FCSTD DOCUMENT  (FreeCAD 0.18.4R)
Label: E3D-V6-Titan-Radial-Fan-Heatbreak-Cooler
License: All rights reserved
LicenseURL: http://en.wikipedia.org/wiki/All_rights_reserved
objects: Sketcher::SketchObject×27, Part::Feature×23, Part::Mirroring×20, PartDesign::Pad×16, PartDesign::Plane×13, PartDesign::Pocket×8, PartDesign::ShapeBinder×8, PartDesign::Body×7, App::Part×5, App::DocumentObjectGroup×3, PartDesign::FeatureBase×3, PartDesign::Fillet×2, Part::Loft×1, PartDesign::AdditiveLoft×1, Mesh::Feature×1, Part::FeaturePython×1
note: 155 computed .brp shape members not serialized (recipe doc carries the construction recipe); baked Part::Feature solids carry a one-line shape summary decoded from their .brp

FEATURE [Sketcher::SketchObject] Sketch
  MapMode = 5
  Support = -> [XY_Plane]
  sketch-geometry (10):
    g0: LineSegment StartX=-15 StartY=15 StartZ=0 EndX=15 EndY=15 EndZ=0
    g1: LineSegment StartX=15 StartY=15 StartZ=0 EndX=15 EndY=-15 EndZ=0
    g2: LineSegment StartX=15 StartY=-15 StartZ=0 EndX=-15 EndY=-15 EndZ=0
    g3: LineSegment StartX=-15 StartY=-15 StartZ=0 EndX=-15 EndY=15 EndZ=0
    g4: LineSegment [constr] StartX=-15 StartY=15 StartZ=0 EndX=15 EndY=-15 EndZ=0
    g5: LineSegment [constr] StartX=15 StartY=15 StartZ=0 EndX=-15 EndY=-15 EndZ=0
    g6: Circle CenterX=-12.125 CenterY=12.125 CenterZ=0 NormalX=0 NormalY=0 NormalZ=1 AngleXU=0 Radius=1.5
    g7: Circle CenterX=12.125 CenterY=12.125 CenterZ=0 NormalX=0 NormalY=0 NormalZ=1 AngleXU=0 Radius=1.5
    g8: Circle CenterX=12.125 CenterY=-12.125 CenterZ=0 NormalX=0 NormalY=0 NormalZ=1 AngleXU=0 Radius=1.5
    g9: Circle CenterX=-12.125 CenterY=-12.125 CenterZ=0 NormalX=0 NormalY=0 NormalZ=1 AngleXU=0 Radius=1.5
  constraints (25):
    c: Coincident(g0,g1)
    c: Coincident(g1,g2)
    c: Coincident(g2,g3)
    c: Coincident(g3,g0)
    c: Horizontal(g2)
    c: Vertical(g1)
    c: Symmetric(g0,g0,g-2)
    c: Symmetric(g2,g0,g-1)
    c: DistanceX(g0,g0) = 30  'Lüfterlänge'
    c: Equal(g3,g0)
    c: Coincident(g4,g0)
    c: Coincident(g4,g1)
    c: Coincident(g5,g0)
    c: Coincident(g5,g2)
    c: PointOnObject(g6,g4)
    c: PointOnObject(g8,g4)
    c: PointOnObject(g9,g5)
    c: Distance(g7,g6) = 24.25
    c: Diameter(g6) = 3
    c: Equal(g6,g7)
    c: Equal(g6,g8)
    c: Equal(g6,g9)
    c: Symmetric(g7,g6,g-2)
    c: Distance(g9,g6) = 24.25
    c: Distance(g8,g9) = 24.25
FEATURE [PartDesign::Pad] Pad
  Length = 12
  Length2 = 100
  Profile = -> Sketch
  Type = 0
FEATURE [Sketcher::SketchObject] Sketch001
  MapMode = 5
  Support = -> [XY_Plane]
  sketch-geometry (1):
    g0: Circle CenterX=0 CenterY=0 CenterZ=0 NormalX=0 NormalY=0 NormalZ=1 AngleXU=0 Radius=13.25
  constraints (2):
    c: Coincident(g0,g-1)
    c: Diameter(g0) = 26.5
FEATURE [PartDesign::Pocket] Pocket
  BaseFeature = -> Pad
  Length = 10
  Length2 = 100
  Profile = -> Sketch001
  Reversed = true
  Type = 0
  expr: Length = Pad.Length - 2mm
FEATURE [PartDesign::Plane] DatumPlane
  AttachmentOffset = pos=(0,0,15) rot=(0,0,1;0rad)
  Length = 35.1381
  MapMode = 5
  Placement = pos=(15,-3.3e-15,3.3e-15) rot=(0.57735,0.57735,0.57735;2.0944rad)
  ResizeMode = 0
  Support = -> [YZ_Plane]
  Width = 27.1381
  expr: AttachmentOffset.Base.z = Sketch.Constraints.Lüfterlänge / 2
FEATURE [Sketcher::SketchObject] Sketch002
  ExternalGeometry = -> [Sketch]
  MapMode = 5
  Placement = pos=(15,-3.3e-15,3.3e-15) rot=(0.57735,0.57735,0.57735;2.0944rad)
  Support = -> [DatumPlane]
  expr: Constraints[9] = Pad.Length - 2 * Constraints.Wandstärke
  sketch-geometry (4):
    g0: LineSegment StartX=-10 StartY=10 StartZ=0 EndX=10 EndY=10 EndZ=0
    g1: LineSegment StartX=10 StartY=10 StartZ=0 EndX=10 EndY=1 EndZ=0
    g2: LineSegment StartX=10 StartY=1 StartZ=0 EndX=-10 EndY=1 EndZ=0
    g3: LineSegment StartX=-10 StartY=1 StartZ=0 EndX=-10 EndY=10 EndZ=0
  constraints (11):
    c: Coincident(g0,g1)
    c: Coincident(g2,g3)
    c: Coincident(g3,g0)
    c: Horizontal(g0)
    c: Vertical(g1)
    c: Vertical(g3)
    c: DistanceX(g2,g2) = 20
    c: Symmetric(g2,g1,g-2)
    c: Coincident(g2,g1)
    c: DistanceY(g-4,g0) = 10
    c: DistanceY(g-3,g1) = 1  'Wandstärke'
FEATURE [PartDesign::Pocket] Pocket001
  BaseFeature = -> Pocket
  Length = 6.5
  Length2 = 100
  Profile = -> Sketch002
  Type = 0
FEATURE [PartDesign::Body] Body  label="30mm-Fan-Adapter"
  Group = -> [Sketch,Pad,Sketch001,Pocket,DatumPlane,Sketch002,Pocket001]
  Origin = -> Origin
  Tip = -> Pocket001
FEATURE [PartDesign::ShapeBinder] ShapeBinder  label="ShapeBinder_30mm_Fan_Adapter"
  Support = -> [Pocket001]
  TraceSupport = false
FEATURE [PartDesign::ShapeBinder] ShapeBinder002
  Placement = pos=(-68,-32,-2e-15) rot=(1,0,0;1.5708rad)
  TraceSupport = false
FEATURE [App::DocumentObjectGroup] Group  label="3rd-party"
FEATURE [Part::Feature] Part__Feature008  label="M_BEARING_MR95ZZ"
  Placement = pos=(22.2171,-38.5563,-4) rot=(0.707107,0.000752,0.707107;3.1431rad)
  shape: bbox 9.742 x 9.742 x 3 mm, 55 faces, 13 solids (baked)
FEATURE [Part::Feature] Part__Feature020  label="ISO 4762 - M3 x 25ISO"
  Placement = pos=(28.5171,-8.05,-25) rot=(0,-1,0;1.5708rad)
  shape: bbox 5.953 x 5.953 x 28 mm, 15 faces (baked)
FEATURE [Part::Mirroring] Part__Mirroring013  label="ISO 4762 - M3 x 25ISO (Mirror #14)"
  Base = (0,0,0)
  Normal = (1,0,0)
  Source = -> Part__Feature020
FEATURE [Part::Feature] Part__Feature009  label="M_BEARING_SMR74ZZ"
  Placement = pos=(22.2171,-38.5563,-20.75) rot=(0,1,0;1.5708rad)
  shape: bbox 9.742 x 9.742 x 3 mm, 55 faces, 13 solids (baked)
FEATURE [Part::Feature] Part__Feature014  label="EX_PIGNION"
  Placement = pos=(6.66075,-23,-0.4) rot=(-0.998967,-0.032133,0.032133;1.57183rad)
  shape: bbox 12.06 x 11.99 x 9 mm, 97 faces (baked)
FEATURE [Part::Feature] Part__Feature003  label="EX_EXTRUDER_LID (Edition 4)_Public"
  Placement = pos=(0.461723,-9.23586,-22) rot=(1,0,0;3.14159rad)
  shape: bbox 46.39 x 49.51 x 137 mm, 484 faces (baked)
FEATURE [Part::Feature] Part__Feature001  label="Spur Gear21"
  Placement = pos=(0,22,0) rot=(0,0,1;3.09399rad)
  shape: bbox 34 x 33.98 x 4 mm, 267 faces (baked)
FEATURE [Part::Mirroring] Part__Mirroring016  label="Spur Gear21 (Mirror #17)"
  Base = (0,0,0)
  Normal = (0,0,1)
  Placement = pos=(-23.13,-60.51,-5.8) rot=(0,0,-1;0.04119rad)
  Source = -> Part__Feature001
FEATURE [Part::Feature] Part__Feature017  label="ISO 4762 - M3 x 20ISO002"
  Placement = pos=(22.1608,-38.5,-25) rot=(0,-1,0;1.5708rad)
  shape: bbox 5.953 x 5.953 x 23 mm, 15 faces (baked)
FEATURE [Part::Feature] Part__Feature018  label="ANSI B18.2.4.2M - M4x0.7 - 7"
  Placement = pos=(-12.4308,-46,-13.5) rot=(1,0,0;2.0944rad)
  shape: bbox 3.8 x 8.083 x 8.083 mm, 23 faces (baked)
FEATURE [Part::Feature] Part__Feature012  label="Titan Idler Tension Screw v6"
  Placement = pos=(-20.0892,-46,-13.5) rot=(0,0,1;0rad)
  shape: bbox 18 x 15 x 15 mm, 12 faces (baked)
FEATURE [Part::Mirroring] Part__Mirroring005  label="Titan Idler Tension Screw v6 (Mirror #6)"
  Base = (0,0,0)
  Normal = (1,0,0)
  Source = -> Part__Feature012
FEATURE [Part::Feature] Part__Feature006  label="EX_EXTRUDER_BODY_2"
  Placement = pos=(6.66075,-23,-1) rot=(1,0,0;3.14159rad)
  shape: bbox 46.57 x 60.21 x 24.06 mm, 338 faces (baked)
FEATURE [Part::Mirroring] Part__Mirroring001  label="EX_EXTRUDER_BODY_2 (Mirror #2)"
  Base = (0,0,0)
  Normal = (1,0,0)
  Source = -> Part__Feature006
FEATURE [Part::Feature] Part__Feature016  label="ISO 4762 - M3 x 20ISO001"
  Placement = pos=(-8.83925,-38.5,-25) rot=(0,-1,0;1.5708rad)
  shape: bbox 5.953 x 5.953 x 23 mm, 15 faces (baked)
FEATURE [Part::Mirroring] Part__Mirroring009  label="ISO 4762 - M3 x 20ISO001 (Mirror #10)"
  Base = (0,0,0)
  Normal = (1,0,0)
  Source = -> Part__Feature016
FEATURE [Part::Feature] Part__Feature013  label="PTFE_HOLDER (Edition 2)"
  Placement = pos=(11.7608,-16.3,-23.5) rot=(-1,-2e-06,-2e-06;1.5708rad)
  shape: bbox 11.22 x 59.29 x 16.4 mm, 201 faces (baked)
FEATURE [Part::Feature] Part__Feature015  label="ISO 4762 - M3 x 20ISO"
  Placement = pos=(-8.83925,-7.5,-25) rot=(0,-1,0;1.5708rad)
  shape: bbox 5.953 x 5.953 x 23 mm, 15 faces (baked)
FEATURE [Part::Mirroring] Part__Mirroring008  label="ISO 4762 - M3 x 20ISO (Mirror #9)"
  Base = (0,0,0)
  Normal = (1,0,0)
  Source = -> Part__Feature015
FEATURE [Part::Feature] Part__Feature019  label="ISO 4762 - M3 x 5ISO"
  Placement = pos=(22.1608,-7.5,-3) rot=(0.447214,-0.774597,0.447214;1.82348rad)
  shape: bbox 5.75 x 5.75 x 8 mm, 15 faces (baked)
FEATURE [Part::Feature] Part__Feature021  label="EX_IDLER_PIN_3mm"
  Placement = pos=(12.2108,-39,-17.5) rot=(0,0,1;0rad)
  shape: bbox 3 x 3 x 8 mm, 8 faces (baked)
FEATURE [Part::Mirroring] Part__Mirroring007  label="EX_PIGNION (Mirror #8)"
  Base = (0,0,0)
  Normal = (1,0,0)
  Source = -> Part__Feature014
FEATURE [Part::Feature] Part__Feature010  label="SOLID001"
  shape: bbox 12.72 x 6.873 x 6.873 mm, 3 faces (baked)
FEATURE [Part::Mirroring] Part__Mirroring017  label="SOLID001 (Mirror #18)"
  Base = (0,0,0)
  Normal = (0,0,1)
  Placement = pos=(8,-45,-13) rot=(0,0,1;0rad)
  Source = -> Part__Feature010
FEATURE [Part::Feature] Part__Feature007  label="IC_EXTRUDER_IDLER_2.1"
  Placement = pos=(6.66075,-23,-11.5) rot=(0.57735,0.57735,-0.57735;4.18879rad)
  shape: bbox 22.05 x 46.43 x 9.747 mm, 528 faces (baked)
FEATURE [Part::Mirroring] Part__Mirroring006  label="PTFE_HOLDER (Edition 2) (Mirror #7)"
  Base = (0,0,0)
  Normal = (1,0,0)
  Source = -> Part__Feature013
FEATURE [Part::Mirroring] Part__Mirroring011  label="ANSI B18.2.4.2M - M4x0.7 - 7 (Mirror #12)"
  Base = (0,0,0)
  Normal = (1,0,0)
  Source = -> Part__Feature018
FEATURE [Part::Mirroring] Part__Mirroring010  label="ISO 4762 - M3 x 20ISO002 (Mirror #11)"
  Base = (0,0,0)
  Normal = (1,0,0)
  Source = -> Part__Feature017
FEATURE [Part::Mirroring] Part__Mirroring014  label="EX_IDLER_PIN_3mm (Mirror #15)"
  Base = (0,0,0)
  Normal = (1,0,0)
  Source = -> Part__Feature021
FEATURE [Part::Mirroring] Part__Mirroring  label="EX_EXTRUDER_LID (Edition 4)_Public (Mirror #1)"
  Base = (0,0,0)
  Normal = (1,0,0)
  Source = -> Part__Feature003
FEATURE [Part::Feature] Part__Feature  label="M_HOBB_v2_EX_Blank"
  Placement = pos=(-22.724,-4.52781,-6.8) rot=(0,0,-1;0.0774rad)
  shape: bbox 10.3 x 10.3 x 20.5 mm, 17 faces (baked)
FEATURE [Part::Mirroring] Part__Mirroring015  label="M_HOBB_v2_EX_Blank (Mirror #16)"
  Base = (0,0,0)
  Normal = (0,0,1)
  Placement = pos=(0.5,-34,-11) rot=(0,0,1;0rad)
  Source = -> Part__Feature
FEATURE [Part::Mirroring] Part__Mirroring002  label="IC_EXTRUDER_IDLER_2.1 (Mirror #3)"
  Base = (0,0,0)
  Normal = (1,0,0)
  Source = -> Part__Feature007
FEATURE [Part::Mirroring] Part__Mirroring004  label="M_BEARING_SMR74ZZ (Mirror #5)"
  Base = (0,0,0)
  Normal = (1,0,0)
  Source = -> Part__Feature009
FEATURE [Part::Mirroring] Part__Mirroring003  label="M_BEARING_MR95ZZ (Mirror #4)"
  Base = (0,0,0)
  Normal = (1,0,0)
  Source = -> Part__Feature008
FEATURE [Part::Mirroring] Part__Mirroring012  label="ISO 4762 - M3 x 5ISO (Mirror #13)"
  Base = (0,0,0)
  Normal = (1,0,0)
  Source = -> Part__Feature019
FEATURE [Part::Feature] Part__Feature011  label="COMPOUND001"
  shape: bbox 1.02 x 2e-07 x 1.02 mm, 0 faces, 0 solids (baked)
FEATURE [Part::Mirroring] Part__Mirroring018  label="COMPOUND001 (Mirror #19)"
  Base = (0,0,0)
  Normal = (0,0,1)
  Source = -> Part__Feature011
FEATURE [App::Part] Part001  label="Titan_gespiegelt"
  Group = -> [Part__Feature003,Part__Mirroring,Part__Feature006,Part__Mirroring001,Part__Feature007,Part__Mirroring002,Part__Feature008,Part__Mirroring003,Part__Feature009,Part__Mirroring004,Part__Feature012,Part__Mirroring005,Part__Feature013,Part__Mirroring006,Part__Feature014,Part__Mirroring007,Part__Feature015,Part__Mirroring008,Part__Feature016,Part__Mirroring009,Part__Feature017,Part__Mirroring010,+16 more]
  License = CC BY 3.0
  LicenseURL = http://creativecommons.org/licenses/by/3.0/
  Origin = -> Origin006
  Placement = pos=(-17.2,-26.2,15) rot=(1,0,0;4.71239rad)
FEATURE [Part::Feature] Fusion001  label="E3DV6_Assembly"
  Placement = pos=(-35.0897,-40.1601,8.5) rot=(0,0.707107,0.707107;3.14159rad)
  shape: bbox 27.55 x 22.3 x 63.4 mm, 442 faces, 3 solids (baked)
FEATURE [Sketcher::SketchObject] Sketch045
  ExternalGeometry = -> [ShapeBinder002]
  MapMode = 5
  Placement = pos=(0,0,0) rot=(1,0,0;1.5708rad)
  Support = -> [XZ_Plane007]
  expr: Constraints[17] = FD_BaseDimension.Constraints.WallThickness_Small
  expr: Constraints[9] = FD_BaseDimension.Constraints.Clearance
  expr: Constraints[20] = FD_BaseDimension.Constraints.WallThickness_Small
  expr: Constraints[18] = FD_BaseDimension.Constraints.WallThickness_Small
  expr: Constraints[8] = FD_BaseDimension.Constraints.Clearance
  expr: Constraints[19] = FD_BaseDimension.Constraints.WallThickness_Small
  expr: Constraints[10] = FD_BaseDimension.Constraints.Clearance
  expr: Constraints[11] = FD_BaseDimension.Constraints.Clearance
  sketch-geometry (8):
    g0: LineSegment StartX=-65.15 StartY=17.4 StartZ=0 EndX=-54.6 EndY=17.4 EndZ=0
    g1: LineSegment StartX=-54.6 StartY=17.4 StartZ=0 EndX=-54.6 EndY=2.85 EndZ=0
    g2: LineSegment StartX=-54.6 StartY=2.85 StartZ=0 EndX=-65.15 EndY=2.85 EndZ=0
    g3: LineSegment StartX=-65.15 StartY=2.85 StartZ=0 EndX=-65.15 EndY=17.4 EndZ=0
    g4: LineSegment StartX=-55.6 StartY=16.4 StartZ=0 EndX=-55.6 EndY=3.85 EndZ=0
    g5: LineSegment StartX=-55.6 StartY=3.85 StartZ=0 EndX=-64.15 EndY=3.85 EndZ=0
    g6: LineSegment StartX=-64.15 StartY=3.85 StartZ=0 EndX=-64.15 EndY=16.4 EndZ=0
    g7: LineSegment StartX=-64.15 StartY=16.4 StartZ=0 EndX=-55.6 EndY=16.4 EndZ=0
  constraints (31):
    c: Coincident(g0,g1)
    c: Coincident(g1,g2)
    c: Coincident(g2,g3)
    c: Coincident(g3,g0)
    c: Horizontal(g0)
    c: Horizontal(g2)
    c: Vertical(g1)
    c: Vertical(g3)
    c: DistanceY(g0,g-4) = 0.6
    c: DistanceX(g-4,g0) = 0.6
    c: DistanceX(g0,g-5) = 0.6
    c: DistanceY(g-6,g2) = 0.6
    c: Coincident(g4,g5)
    c: Coincident(g5,g6)
    c: Horizontal(g5)
    c: Vertical(g4)
    c: Vertical(g6)
    c: DistanceX(g2,g5) = 1
    c: DistanceY(g2,g5) = 1
    c: DistanceX(g4,g1) = 1
    c: DistanceY(g6,g0) = 1
    c: Coincident(g7,g6)
    c: Coincident(g7,g4)
    c: Horizontal(g7)
    c: Distance(g0) = 10.55
    c: Distance(g7) = 8.55
    c: Distance(g4) = 12.55
    c: Distance(g-3) = 11.75
    c: Distance(g-5) = 15.75
    c: Distance(g4) = 12.55
    c: Distance(g1) = 14.55
FEATURE [PartDesign::Pad] Pad020  label="SnugglyFit_ToClamp"
  Length = 10
  Length2 = 100
  Placement = pos=(0,0,0) rot=(1,0,0;1.5708rad)
  Profile = -> Sketch045
  Reversed = true
  Type = 0
FEATURE [Sketcher::SketchObject] Sketch053  label="FD_BaseDimension"
  MapMode = 5
  Placement = pos=(0,0,0) rot=(1,0,0;1.5708rad)
  Support = -> [XZ_Plane007]
  sketch-geometry (3):
    g0: LineSegment [constr] StartX=-77.6491 StartY=47.6557 StartZ=0 EndX=-76.6491 EndY=47.6557 EndZ=0
    g1: LineSegment [constr] StartX=-78.0014 StartY=44.3485 StartZ=0 EndX=-77.4014 EndY=44.3485 EndZ=0
    g2: LineSegment [constr] StartX=-73.0784 StartY=47.1247 StartZ=0 EndX=-72.0784 EndY=47.1247 EndZ=0
  constraints (6):
    c: Horizontal(g0)
    c: DistanceX(g0,g0) = 1  'WallThickness_Regular'
    c: Horizontal(g1)
    c: DistanceX(g1,g1) = 0.6  'Clearance'
    c: Horizontal(g2)
    c: DistanceX(g2,g2) = 1  'WallThickness_Small'
FEATURE [PartDesign::Plane] DatumPlane022  label="PrintSurface"
  AttachmentOffset = pos=(0,0,0) rot=(0,1,0;1.5708rad)
  Length = 63.2526
  MapMode = 7
  Placement = pos=(-65.15,-2.936e-13,2.85) rot=(0,1,0;4.71239rad)
  ResizeMode = 0
  Support = -> [Sketch045]
  Width = 51.5026
FEATURE [Sketcher::SketchObject] Sketch046
  ExternalGeometry = -> [ShapeBinder002,Sketch045,DatumPlane022]
  MapMode = 5
  Placement = pos=(0,0,0) rot=(1,0,0;1.5708rad)
  Support = -> [XZ_Plane007]
  sketch-geometry (9):
    g0: LineSegment StartX=-65.15 StartY=18 StartZ=0 EndX=-52.4 EndY=18 EndZ=0
    g1: LineSegment StartX=-50.15 StartY=15.75 StartZ=0 EndX=-50.15 EndY=-5.75 EndZ=0
    g2: LineSegment StartX=-50.15 StartY=-5.75 StartZ=0 EndX=-65.15 EndY=-5.75 EndZ=0
    g3: LineSegment StartX=-65.15 StartY=-5.75 StartZ=0 EndX=-65.15 EndY=18 EndZ=0
    g4: LineSegment StartX=-64.15 StartY=3.85 StartZ=0 EndX=-55.6 EndY=3.85 EndZ=0
    g5: LineSegment StartX=-55.6 StartY=3.85 StartZ=0 EndX=-55.6 EndY=16.4 EndZ=0
    g6: LineSegment StartX=-55.6 StartY=16.4 StartZ=0 EndX=-64.15 EndY=16.4 EndZ=0
    g7: LineSegment StartX=-64.15 StartY=16.4 StartZ=0 EndX=-64.15 EndY=3.85 EndZ=0
    g8: LineSegment StartX=-52.4 StartY=18 StartZ=0 EndX=-50.15 EndY=15.75 EndZ=0
  constraints (25):
    c: Coincident(g1,g2)
    c: Coincident(g2,g3)
    c: Horizontal(g0)
    c: Horizontal(g2)
    c: Vertical(g1)
    c: Vertical(g3)
    c: Coincident(g4,g5)
    c: Coincident(g5,g6)
    c: Coincident(g6,g7)
    c: Coincident(g7,g4)
    c: Horizontal(g4)
    c: Horizontal(g6)
    c: Vertical(g5)
    c: Vertical(g7)
    c: Coincident(g0,g3)
    c: Coincident(g6,g-8)
    c: Coincident(g-7,g4)
    c: PointOnObject(g-5,g0)
    c: Coincident(g0,g8)
    c: Coincident(g8,g1)
    c: Angle(g8,g1) = 2.35619
    c: DistanceX(g0,g0) = 12.75
    c: DistanceY(g1,g1) = 21.5
    c: DistanceY(g3,g3) = 23.75
    c: PointOnObject(g0,g-10)
FEATURE [PartDesign::Pad] Pad021  label="FD_MakeItBigger"
  BaseFeature = -> Pad020
  Length = 1
  Length2 = 100
  Placement = pos=(0,0,0) rot=(1,0,0;1.5708rad)
  Profile = -> Sketch046
  Type = 0
FEATURE [PartDesign::Plane] DatumPlane016  label="FrontBiggerMakerPlate"
  AttachmentOffset = pos=(0,0,1) rot=(0,0,1;0rad)
  Length = 88.5118
  MapMode = 2
  Placement = pos=(0,-1,-1.031e-13) rot=(1,0,0;1.5708rad)
  ResizeMode = 0
  Support = -> [Sketch046]
  Width = 66.5118
  expr: AttachmentOffset.Base.z = Pad021.Length
FEATURE [Sketcher::SketchObject] Sketch047
  ExternalGeometry = -> [DatumPlane022,Sketch046]
  MapMode = 5
  Placement = pos=(0,-1,-1.031e-13) rot=(1,0,0;1.5708rad)
  Support = -> [DatumPlane016]
  expr: Constraints[29] = FD_BaseDimension.Constraints.WallThickness_Regular
  expr: Constraints[22] = FD_BaseDimension.Constraints.WallThickness_Regular
  expr: Constraints[21] = FD_BaseDimension.Constraints.WallThickness_Regular
  expr: Constraints[23] = FD_BaseDimension.Constraints.WallThickness_Regular
  expr: Constraints[19] = FD_BaseDimension.Constraints.WallThickness_Small
  sketch-geometry (11):
    g0: LineSegment StartX=-65.15 StartY=18 StartZ=0 EndX=-52.4 EndY=18 EndZ=0
    g1: LineSegment StartX=-50.15 StartY=15.75 StartZ=0 EndX=-50.15 EndY=-5.75 EndZ=0
    g2: LineSegment StartX=-50.15 StartY=-5.75 StartZ=0 EndX=-65.15 EndY=-5.75 EndZ=0
    g3: LineSegment StartX=-65.15 StartY=-5.75 StartZ=0 EndX=-65.15 EndY=18 EndZ=0
    g4: LineSegment StartX=-64.15 StartY=17 StartZ=0 EndX=-52.8142 EndY=17 EndZ=0
    g5: LineSegment StartX=-51.15 StartY=15.3358 StartZ=0 EndX=-51.15 EndY=-4.75 EndZ=0
    g6: LineSegment StartX=-51.15 StartY=-4.75 StartZ=0 EndX=-64.15 EndY=-4.75 EndZ=0
    g7: LineSegment StartX=-64.15 StartY=-4.75 StartZ=0 EndX=-64.15 EndY=17 EndZ=0
    g8: LineSegment StartX=-52.8142 StartY=17 StartZ=0 EndX=-51.15 EndY=15.3358 EndZ=0
    g9: LineSegment StartX=-52.4 StartY=18 StartZ=0 EndX=-50.15 EndY=15.75 EndZ=0
    g10: LineSegment [constr] StartX=-52.8142 StartY=17 StartZ=0 EndX=-52.1071 EndY=17.7071 EndZ=0
  constraints (31):
    c: Coincident(g1,g2)
    c: Coincident(g2,g3)
    c: Coincident(g3,g0)
    c: Horizontal(g0)
    c: Horizontal(g2)
    c: Vertical(g1)
    c: Vertical(g3)
    c: Coincident(g5,g6)
    c: Coincident(g6,g7)
    c: Coincident(g7,g4)
    c: Horizontal(g4)
    c: Horizontal(g6)
    c: Vertical(g5)
    c: Vertical(g7)
    c: PointOnObject(g0,g-3)
    c: Coincident(g8,g4)
    c: Coincident(g8,g5)
    c: Coincident(g9,g0)
    c: Parallel(g8,g9)
    c: DistanceX(g0,g4) = 1
    c: Coincident(g9,g1)
    c: DistanceY(g2,g6) = 1
    c: DistanceX(g5,g1) = 1
    c: DistanceY(g4,g0) = 1
    c: Coincident(g0,g-4)
    c: Coincident(g1,g-4)
    c: Coincident(g10,g4)
    c: PointOnObject(g10,g9)
    c: Perpendicular(g10,g9)
    c: Distance(g10) = 1
    c: PointOnObject(g-5,g2)
FEATURE [PartDesign::Pad] Pad022  label="FanDuct_Horizontal1"
  BaseFeature = -> Pad021
  Length = 18
  Length2 = 100
  Placement = pos=(0,0,0) rot=(1,0,0;1.5708rad)
  Profile = -> Sketch047
  Type = 0
FEATURE [PartDesign::Plane] DatumPlane017  label="FD_H1_FrontPlane"
  AttachmentOffset = pos=(0,0,18) rot=(0,0,1;0rad)
  Length = 88.5118
  MapMode = 2
  Placement = pos=(0,-19,-1.9586e-12) rot=(1,0,0;1.5708rad)
  ResizeMode = 0
  Support = -> [Sketch047]
  Width = 66.5118
  expr: AttachmentOffset.Base.z = Pad022.Length
FEATURE [Sketcher::SketchObject] Sketch054
  ExternalGeometry = -> [DatumPlane022,Sketch046]
  MapMode = 5
  Placement = pos=(0,-19,-1.9586e-12) rot=(1,0,0;1.5708rad)
  Support = -> [DatumPlane017]
  expr: Constraints[42] = FD_BaseDimension.Constraints.WallThickness_Regular
  expr: Constraints[43] = FD_BaseDimension.Constraints.WallThickness_Regular
  expr: Constraints[18] = FD_BaseDimension.Constraints.WallThickness_Regular
  expr: Constraints[17] = FD_BaseDimension.Constraints.WallThickness_Regular
  expr: Constraints[16] = FD_BaseDimension.Constraints.WallThickness_Regular
  expr: Constraints[15] = FD_BaseDimension.Constraints.WallThickness_Small
  sketch-geometry (15):
    g0: LineSegment StartX=-65.15 StartY=18 StartZ=0 EndX=-50.15 EndY=18 EndZ=0
    g1: LineSegment StartX=-50.15 StartY=-5.75 StartZ=0 EndX=-65.15 EndY=-5.75 EndZ=0
    g2: LineSegment StartX=-65.15 StartY=-5.75 StartZ=0 EndX=-65.15 EndY=18 EndZ=0
    g3: LineSegment StartX=-64.15 StartY=17 StartZ=0 EndX=-52.8142 EndY=17 EndZ=0
    g4: LineSegment StartX=-51.15 StartY=15.3358 StartZ=0 EndX=-51.15 EndY=-4.75 EndZ=0
    g5: LineSegment StartX=-51.15 StartY=-4.75 StartZ=0 EndX=-64.15 EndY=-4.75 EndZ=0
    g6: LineSegment StartX=-64.15 StartY=-4.75 StartZ=0 EndX=-64.15 EndY=17 EndZ=0
    g7: LineSegment StartX=-52.8142 StartY=17 StartZ=0 EndX=-51.15 EndY=15.3358 EndZ=0
    g8: LineSegment [constr] StartX=-52.8142 StartY=17 StartZ=0 EndX=-52.1071 EndY=17.7071 EndZ=0
    g9: LineSegment StartX=-50.15 StartY=-5.75 StartZ=0 EndX=-50.15 EndY=-2.6 EndZ=0
    g10: LineSegment StartX=-50.15 StartY=-2.6 StartZ=0 EndX=-41.15 EndY=-2.6 EndZ=0
    g11: LineSegment StartX=-41.15 StartY=-2.6 StartZ=0 EndX=-41.15 EndY=4.9 EndZ=0
    g12: LineSegment StartX=-41.15 StartY=4.9 StartZ=0 EndX=-50.15 EndY=4.9 EndZ=0
    g13: LineSegment StartX=-50.15 StartY=4.9 StartZ=0 EndX=-50.15 EndY=18 EndZ=0
    g14: Circle CenterX=-45.65 CenterY=1.05 CenterZ=0 NormalX=0 NormalY=0 NormalZ=1 AngleXU=0 Radius=2
  constraints (45):
    c: Coincident(g1,g2)
    c: Coincident(g2,g0)
    c: Horizontal(g0)
    c: Horizontal(g1)
    c: Vertical(g2)
    c: Coincident(g4,g5)
    c: Coincident(g5,g6)
    c: Coincident(g6,g3)
    c: Horizontal(g3)
    c: Horizontal(g5)
    c: Vertical(g4)
    c: Vertical(g6)
    c: PointOnObject(g0,g-3)
    c: Coincident(g7,g3)
    c: Coincident(g7,g4)
    c: DistanceX(g0,g3) = 1
    c: DistanceY(g1,g5) = 1
    c: DistanceX(g4,g1) = 1
    c: DistanceY(g3,g0) = 1
    c: Coincident(g8,g3)
    c: PointOnObject(g-5,g1)
    c: Coincident(g9,g1)
    c: Vertical(g9)
    c: Horizontal(g10)
    c: Coincident(g10,g11)
    c: Vertical(g11)
    c: Coincident(g11,g12)
    c: Horizontal(g12)
    c: Coincident(g12,g13)
    c: Vertical(g13)
    c: Equal(g10,g12)
    c: DistanceY(g11,g11) = 7.5
    c: Coincident(g10,g9)
    c: DistanceX(g9,g14) = 4.5
    c: DistanceY(g9,g14) = 3.65
    c: DistanceX(g12,g12) = 9
    c: Radius(g14) = 2
    c: DistanceY(g9,g9) = 3.15
    c: PointOnObject(g-4,g0)
    c: Coincident(g0,g13)
    c: PointOnObject(g8,g-4)
    c: Perpendicular(g8,g-4)
    c: DistanceX(g4,g-4) = 1
    c: Distance(g8) = 1
    c: Parallel(g7,g-4)
FEATURE [PartDesign::Pad] Pad026  label="FD_ScrewingTab"
  BaseFeature = -> Pad022
  Length = 2
  Length2 = 100
  Placement = pos=(0,0,0) rot=(1,0,0;1.5708rad)
  Profile = -> Sketch054
  Type = 0
FEATURE [PartDesign::Plane] DatumPlane023  label="FD_FrontOfScrewingTabPlane"
  AttachmentOffset = pos=(0,0,2) rot=(0,0,1;0rad)
  Length = 88.5118
  MapMode = 2
  Placement = pos=(0,-21,-2.1652e-12) rot=(1,0,0;1.5708rad)
  ResizeMode = 0
  Support = -> [Sketch054]
  Width = 66.5118
  expr: AttachmentOffset.Base.z = FD_ScrewingTab.Length
FEATURE [PartDesign::Plane] DatumPlane024  label="Opposite_From_PrintSurface"
  AttachmentOffset = pos=(0,0,0) rot=(0,1,0;1.5708rad)
  Length = 63.2526
  MapMode = 7
  Placement = pos=(-50.15,-1.6227e-12,15.75) rot=(0,1,0;4.71239rad)
  ResizeMode = 0
  Support = -> [Sketch046]
  Width = 51.5026
FEATURE [PartDesign::Plane] DatumPlane025  label="Bottom_Plane"
  AttachmentOffset = pos=(0,0,0) rot=(1,0,0;1.5708rad)
  Length = 53.281
  MapMode = 7
  Placement = pos=(-50.15,5.924e-13,-5.75) rot=(0.707107,0.707107,0;3.14159rad)
  ResizeMode = 0
  Support = -> [Sketch046]
  Width = 87.031
FEATURE [Sketcher::SketchObject] Sketch055
  ExternalGeometry = -> [DatumPlane023,Sketch054,DatumPlane025]
  MapMode = 5
  Placement = pos=(-65.15,-2.936e-13,2.85) rot=(0,-1,0;1.5708rad)
  Support = -> [DatumPlane022]
  expr: Constraints[25] = FD_BaseDimension.Constraints.WallThickness_Regular
  expr: Constraints[17] = FD_BaseDimension.Constraints.WallThickness_Regular
  sketch-geometry (10):
    g0: LineSegment StartX=-8.6 StartY=-21 StartZ=0 EndX=-8.6 EndY=-31.5 EndZ=0
    g1: LineSegment StartX=-8.6 StartY=-31.5 StartZ=0 EndX=5.15 EndY=-31.5 EndZ=0
    g2: LineSegment StartX=15.15 StartY=-21.5 StartZ=0 EndX=15.15 EndY=-21 EndZ=0
    g3: ArcOfCircle CenterX=5.15 CenterY=-21.5 CenterZ=0 NormalX=0 NormalY=0 NormalZ=1 AngleXU=0 Radius=10 StartAngle=4.71239 EndAngle=6.28319
    g4: LineSegment StartX=-7.6 StartY=-21 StartZ=0 EndX=-7.6 EndY=-30.5 EndZ=0
    g5: LineSegment StartX=-7.6 StartY=-30.5 StartZ=0 EndX=5.15 EndY=-30.5 EndZ=0
    g6: ArcOfCircle CenterX=5.15 CenterY=-21.5 CenterZ=0 NormalX=0 NormalY=0 NormalZ=1 AngleXU=0 Radius=9 StartAngle=4.71239 EndAngle=6.28318
    g7: LineSegment StartX=-7.6 StartY=-21 StartZ=0 EndX=-8.6 EndY=-21 EndZ=0
    g8: LineSegment StartX=14.15 StartY=-21 StartZ=0 EndX=15.15 EndY=-21 EndZ=0
    g9: LineSegment StartX=14.15 StartY=-21 StartZ=0 EndX=14.15 EndY=-21.5 EndZ=0
  constraints (29):
    c: Horizontal(g1)
    c: Vertical(g0)
    c: Vertical(g2)
    c: Tangent(g2,g3) = -1.5708
    c: Tangent(g1,g3) = -1.5708
    c: Horizontal(g5)
    c: Coincident(g6,g3)
    c: Coincident(g5,g4)
    c: Coincident(g7,g4)
    c: Coincident(g7,g0)
    c: Horizontal(g7)
    c: Coincident(g5,g6)
    c: Radius(g3) = 10
    c: Radius(g6) = 9
    c: Coincident(g8,g2)
    c: Horizontal(g8)
    c: PointOnObject(g-6,g2)
    c: DistanceX(g8,g8) = 1
    c: Coincident(g9,g8)
    c: Coincident(g9,g6)
    c: Vertical(g9)
    c: DistanceY(g2,g2) = 0.5
    c: PointOnObject(g2,g-3)
    c: Coincident(g0,g1)
    c: Vertical(g4)
    c: DistanceX(g7,g7) = 1
    c: PointOnObject(g0,g-3)
    c: PointOnObject(g0,g-7)
    c: DistanceY(g0,g4) = 1
FEATURE [PartDesign::Pad] Pad027  label="FD_Curve"
  BaseFeature = -> Pad026
  Length = 10
  Length2 = 100
  Placement = pos=(0,0,0) rot=(1,0,0;1.5708rad)
  Profile = -> Sketch055
  Reversed = true
  Type = 3
  UpToFace = -> DatumPlane024 [Plane]
FEATURE [Sketcher::SketchObject] Sketch057
  ExternalGeometry = -> [Pad027,Sketch055]
  MapMode = 5
  Placement = pos=(-50.15,-1.6227e-12,15.75) rot=(0,-1,0;1.5708rad)
  Support = -> [DatumPlane024]
  sketch-geometry (5):
    g0: LineSegment StartX=2.25 StartY=-21 StartZ=0 EndX=2.25 EndY=-21.5 EndZ=0
    g1: LineSegment StartX=-7.75 StartY=-31.5 StartZ=0 EndX=-21.5 EndY=-31.5 EndZ=0
    g2: LineSegment StartX=-21.5 StartY=-31.5 StartZ=0 EndX=-21.5 EndY=-21 EndZ=0
    g3: LineSegment StartX=-21.5 StartY=-21 StartZ=0 EndX=2.25 EndY=-21 EndZ=0
    g4: ArcOfCircle CenterX=-7.75 CenterY=-21.5 CenterZ=0 NormalX=0 NormalY=0 NormalZ=1 AngleXU=0 Radius=10 StartAngle=4.71239 EndAngle=6.28319
  constraints (11):
    c: Coincident(g0,g-6)
    c: Vertical(g0)
    c: Horizontal(g1)
    c: Coincident(g1,g2)
    c: Coincident(g2,g-4)
    c: Vertical(g2)
    c: Coincident(g2,g3)
    c: Coincident(g3,g0)
    c: Tangent(g0,g4) = 1.5708
    c: Tangent(g1,g4) = 1.5708
    c: Coincident(g4,g-5)
FEATURE [PartDesign::Pad] Pad028  label="FD_CurveLID"
  BaseFeature = -> Pad027
  Length = 1
  Length2 = 100
  Placement = pos=(0,0,0) rot=(1,0,0;1.5708rad)
  Profile = -> Sketch057
  Type = 0
  expr: Length = FD_BaseDimension.Constraints.WallThickness_Regular
FEATURE [Sketcher::SketchObject] Sketch058
  ExternalGeometry = -> [Sketch055]
  MapMode = 5
  Placement = pos=(-65.15,-2.936e-13,2.85) rot=(0,-1,0;1.5708rad)
  Support = -> [DatumPlane022]
  sketch-geometry (5):
    g0: LineSegment StartX=15.15 StartY=-21 StartZ=0 EndX=15.15 EndY=-21.5 EndZ=0
    g1: LineSegment StartX=5.15 StartY=-31.5 StartZ=0 EndX=-8.6 EndY=-31.5 EndZ=0
    g2: LineSegment StartX=-8.6 StartY=-31.5 StartZ=0 EndX=-8.6 EndY=-21 EndZ=0
    g3: LineSegment StartX=-8.6 StartY=-21 StartZ=0 EndX=15.15 EndY=-21 EndZ=0
    g4: ArcOfCircle CenterX=5.15 CenterY=-21.5 CenterZ=0 NormalX=0 NormalY=0 NormalZ=1 AngleXU=0 Radius=10 StartAngle=4.71239 EndAngle=6.28319
  constraints (11):
    c: Vertical(g0)
    c: Horizontal(g1)
    c: Coincident(g1,g2)
    c: Vertical(g2)
    c: Coincident(g2,g3)
    c: Coincident(g3,g0)
    c: Tangent(g0,g4) = 1.5708
    c: Tangent(g1,g4) = 1.5708
    c: Coincident(g4,g-4)
    c: Coincident(g2,g-3)
    c: Coincident(g-5,g0)
FEATURE [PartDesign::Pad] Pad029  label="CureveLID2"
  BaseFeature = -> Pad028
  Length = 1
  Length2 = 100
  Placement = pos=(0,0,0) rot=(1,0,0;1.5708rad)
  Profile = -> Sketch058
  Reversed = true
  Type = 0
  expr: Length = FD_BaseDimension.Constraints.WallThickness_Small
FEATURE [Sketcher::SketchObject] Sketch059
  ExternalGeometry = -> [Pad029,Sketch057]
  MapMode = 5
  Placement = pos=(-50.15,5.924e-13,-5.75) rot=(0.707107,0.707107,0;3.14159rad)
  Support = -> [DatumPlane025]
  expr: Constraints[10] = 1.5 * FD_BaseDimension.Constraints.WallThickness_Regular
  expr: Constraints[9] = FD_BaseDimension.Constraints.WallThickness_Small
  expr: Constraints[8] = FD_BaseDimension.Constraints.WallThickness_Regular
  sketch-geometry (4):
    g0: LineSegment StartX=-3 StartY=-1 StartZ=0 EndX=-30 EndY=-1 EndZ=0
    g1: LineSegment StartX=-30 StartY=-1 StartZ=0 EndX=-30 EndY=-14 EndZ=0
    g2: LineSegment StartX=-30 StartY=-14 StartZ=0 EndX=-3 EndY=-14 EndZ=0
    g3: LineSegment StartX=-3 StartY=-14 StartZ=0 EndX=-3 EndY=-1 EndZ=0
  constraints (12):
    c: Coincident(g0,g1)
    c: Coincident(g1,g2)
    c: Coincident(g2,g3)
    c: Coincident(g3,g0)
    c: Horizontal(g0)
    c: Horizontal(g2)
    c: Vertical(g1)
    c: Vertical(g3)
    c: DistanceY(g0,g-4) = 1
    c: DistanceY(g-3,g2) = 1
    c: DistanceX(g-3,g1) = 1.5
    c: DistanceX(g2,g2) = 27
FEATURE [PartDesign::Pocket] Pocket007015
  BaseFeature = -> Pad029
  Length = 5
  Length2 = 100
  Placement = pos=(0,0,0) rot=(1,0,0;1.5708rad)
  Profile = -> Sketch059
  Type = 0
FEATURE [Sketcher::SketchObject] Sketch060  label="InterfaceToDüse"
  ExternalGeometry = -> [Sketch059]
  MapMode = 5
  Placement = pos=(-50.15,5.924e-13,-5.75) rot=(0.707107,0.707107,0;3.14159rad)
  Support = -> [DatumPlane025]
  expr: Constraints[20] = FD_BaseDimension.Constraints.WallThickness_Small
  expr: Constraints[19] = 2 * FD_BaseDimension.Constraints.WallThickness_Regular
  expr: Constraints[18] = FD_BaseDimension.Constraints.WallThickness_Regular
  expr: Constraints[16] = 1.5 * FD_BaseDimension.Constraints.WallThickness_Regular
  sketch-geometry (8):
    g0: LineSegment StartX=-31.5 StartY=0 StartZ=0 EndX=-1 EndY=0 EndZ=0
    g1: LineSegment StartX=-1 StartY=0 StartZ=0 EndX=-1 EndY=-15 EndZ=0
    g2: LineSegment StartX=-1 StartY=-15 StartZ=0 EndX=-31.5 EndY=-15 EndZ=0
    g3: LineSegment StartX=-31.5 StartY=-15 StartZ=0 EndX=-31.5 EndY=0 EndZ=0
    g4: LineSegment StartX=-30 StartY=-1 StartZ=0 EndX=-3 EndY=-1 EndZ=0
    g5: LineSegment StartX=-3 StartY=-1 StartZ=0 EndX=-3 EndY=-14 EndZ=0
    g6: LineSegment StartX=-3 StartY=-14 StartZ=0 EndX=-30 EndY=-14 EndZ=0
    g7: LineSegment StartX=-30 StartY=-14 StartZ=0 EndX=-30 EndY=-1 EndZ=0
  constraints (22):
    c: Coincident(g0,g1)
    c: Coincident(g1,g2)
    c: Coincident(g2,g3)
    c: Coincident(g3,g0)
    c: Horizontal(g0)
    c: Horizontal(g2)
    c: Vertical(g1)
    c: Vertical(g3)
    c: Coincident(g4,g5)
    c: Coincident(g5,g6)
    c: Coincident(g6,g7)
    c: Coincident(g7,g4)
    c: Horizontal(g4)
    c: Horizontal(g6)
    c: Vertical(g5)
    c: Vertical(g7)
    c: DistanceX(g2,g6) = 1.5
    c: Coincident(g6,g-5)
    c: DistanceY(g4,g0) = 1
    c: DistanceX(g4,g0) = 2
    c: DistanceY(g1,g5) = 1
    c: Coincident(g-6,g4)
FEATURE [PartDesign::ShapeBinder] ShapeBinder003
  Placement = pos=(-50.15,5.95e-13,-5.75) rot=(0.707107,0.707107,0;3.14159rad)
  Support = -> [Sketch060]
  TraceSupport = false
FEATURE [PartDesign::Pad] Pad030  label="Fanduct_Part1"
  BaseFeature = -> Pocket007015
  Length = 30
  Length2 = 100
  Placement = pos=(0,0,0) rot=(1,0,0;1.5708rad)
  Profile = -> Sketch060
  Type = 0
FEATURE [PartDesign::Fillet] Fillet
  Base = -> Pad030 [Edge50,Edge138]
  BaseFeature = -> Pad030
  Placement = pos=(0,0,0) rot=(1,0,0;1.5708rad)
  Radius = 2
FEATURE [PartDesign::Body] Body003  label="Fanduct_Duct"
  Group = -> [ShapeBinder002,Sketch053,DatumPlane022,DatumPlane024,DatumPlane025,Sketch045,Pad020,Sketch046,Pad021,DatumPlane016,Sketch047,Pad022,DatumPlane017,Sketch054,Pad026,DatumPlane023,Sketch055,Pad027,Sketch057,Pad028,Sketch058,Pad029,Sketch059,Pocket007015,Sketch060,Pad030,Fillet]
  Origin = -> Origin007
  Placement = pos=(0,-32,22) rot=(0,0,1;0rad)
  Tip = -> Fillet
FEATURE [Sketcher::SketchObject] Sketch061
  ExternalGeometry = -> [ShapeBinder003]
  MapMode = 5
  Support = -> [XY_Plane008]
  expr: Constraints[23] = FD_BaseDimension.Constraints.WallThickness_Small
  expr: Constraints[21] = FD_BaseDimension.Constraints.WallThickness_Small
  expr: Constraints[20] = FD_BaseDimension.Constraints.WallThickness_Small
  expr: Constraints[11] = FD_BaseDimension.Constraints.Clearance
  expr: Constraints[10] = FD_BaseDimension.Constraints.Clearance
  expr: Constraints[22] = FD_BaseDimension.Constraints.WallThickness_Small
  expr: Constraints[9] = FD_BaseDimension.Constraints.Clearance
  expr: Constraints[8] = FD_BaseDimension.Constraints.Clearance
  sketch-geometry (8):
    g0: LineSegment StartX=-63.55 StartY=-3.6 StartZ=0 EndX=-51.75 EndY=-3.6 EndZ=0
    g1: LineSegment StartX=-51.75 StartY=-3.6 StartZ=0 EndX=-51.75 EndY=-29.4 EndZ=0
    g2: LineSegment StartX=-51.75 StartY=-29.4 StartZ=0 EndX=-63.55 EndY=-29.4 EndZ=0
    g3: LineSegment StartX=-63.55 StartY=-29.4 StartZ=0 EndX=-63.55 EndY=-3.6 EndZ=0
    g4: LineSegment StartX=-62.55 StartY=-4.6 StartZ=0 EndX=-52.75 EndY=-4.6 EndZ=0
    g5: LineSegment StartX=-52.75 StartY=-4.6 StartZ=0 EndX=-52.75 EndY=-28.4 EndZ=0
    g6: LineSegment StartX=-52.75 StartY=-28.4 StartZ=0 EndX=-62.55 EndY=-28.4 EndZ=0
    g7: LineSegment StartX=-62.55 StartY=-28.4 StartZ=0 EndX=-62.55 EndY=-4.6 EndZ=0
  constraints (24):
    c: Coincident(g0,g1)
    c: Coincident(g1,g2)
    c: Coincident(g2,g3)
    c: Coincident(g3,g0)
    c: Horizontal(g0)
    c: Horizontal(g2)
    c: Vertical(g1)
    c: Vertical(g3)
    c: DistanceX(g-6,g2) = 0.6
    c: DistanceY(g-6,g2) = 0.6
    c: DistanceY(g0,g-5) = 0.6
    c: DistanceX(g0,g-5) = 0.6
    c: Coincident(g4,g5)
    c: Coincident(g5,g6)
    c: Coincident(g6,g7)
    c: Coincident(g7,g4)
    c: Horizontal(g4)
    c: Horizontal(g6)
    c: Vertical(g5)
    c: Vertical(g7)
    c: DistanceX(g0,g4) = 1
    c: DistanceY(g4,g0) = 1
    c: DistanceY(g1,g5) = 1
    c: DistanceX(g5,g1) = 1
FEATURE [PartDesign::Pad] Pad031
  Length = 15
  Length2 = 100
  Profile = -> Sketch061
  Type = 0
FEATURE [Sketcher::SketchObject] Sketch062
  ExternalGeometry = -> [Sketch061,ShapeBinder003]
  MapMode = 5
  Support = -> [XY_Plane008]
  sketch-geometry (8):
    g0: LineSegment StartX=-52.75 StartY=-4.6 StartZ=0 EndX=-62.55 EndY=-4.6 EndZ=0
    g1: LineSegment StartX=-62.55 StartY=-4.6 StartZ=0 EndX=-62.55 EndY=-28.4 EndZ=0
    g2: LineSegment StartX=-62.55 StartY=-28.4 StartZ=0 EndX=-52.75 EndY=-28.4 EndZ=0
    g3: LineSegment StartX=-52.75 StartY=-28.4 StartZ=0 EndX=-52.75 EndY=-4.6 EndZ=0
    g4: LineSegment StartX=-65.15 StartY=-31.5 StartZ=0 EndX=-50.15 EndY=-31.5 EndZ=0
    g5: LineSegment StartX=-50.15 StartY=-31.5 StartZ=0 EndX=-50.15 EndY=-1 EndZ=0
    g6: LineSegment StartX=-50.15 StartY=-1 StartZ=0 EndX=-65.15 EndY=-1 EndZ=0
    g7: LineSegment StartX=-65.15 StartY=-1 StartZ=0 EndX=-65.15 EndY=-31.5 EndZ=0
  constraints (20):
    c: Coincident(g0,g1)
    c: Coincident(g1,g2)
    c: Coincident(g2,g3)
    c: Coincident(g3,g0)
    c: Horizontal(g0)
    c: Horizontal(g2)
    c: Vertical(g1)
    c: Vertical(g3)
    c: Coincident(g0,g-3)
    c: Coincident(g1,g-4)
    c: Coincident(g4,g5)
    c: Coincident(g5,g6)
    c: Coincident(g6,g7)
    c: Coincident(g7,g4)
    c: Horizontal(g4)
    c: Horizontal(g6)
    c: Vertical(g5)
    c: Vertical(g7)
    c: Coincident(g6,g-5)
    c: Coincident(g-6,g4)
FEATURE [PartDesign::Pad] Pad032
  BaseFeature = -> Pad031
  Length = 1
  Length2 = 100
  Profile = -> Sketch062
  Reversed = true
  Type = 0
FEATURE [PartDesign::Plane] DatumPlane026  label="Pad032_Plane"
  AttachmentOffset = pos=(0,0,-1) rot=(0,0,1;0rad)
  Length = 86.3191
  MapMode = 2
  Placement = pos=(0,0,1) rot=(0,1,0;3.14159rad)
  ResizeMode = 0
  Support = -> [Sketch062]
  Width = 52.6691
  expr: AttachmentOffset.Base.z = -Pad032.Length
FEATURE [Sketcher::SketchObject] Sketch063
  ExternalGeometry = -> [Sketch062]
  MapMode = 5
  Placement = pos=(0,0,1) rot=(0,1,0;3.14159rad)
  Support = -> [DatumPlane026]
  expr: Constraints[21] = FD_BaseDimension.Constraints.WallThickness_Regular
  expr: Constraints[20] = FD_BaseDimension.Constraints.WallThickness_Regular
  expr: Constraints[19] = FD_BaseDimension.Constraints.WallThickness_Regular
  expr: Constraints[18] = FD_BaseDimension.Constraints.WallThickness_Regular
  sketch-geometry (8):
    g0: LineSegment StartX=50.15 StartY=-1 StartZ=0 EndX=65.15 EndY=-1 EndZ=0
    g1: LineSegment StartX=65.15 StartY=-1 StartZ=0 EndX=65.15 EndY=-31.5 EndZ=0
    g2: LineSegment StartX=65.15 StartY=-31.5 StartZ=0 EndX=50.15 EndY=-31.5 EndZ=0
    g3: LineSegment StartX=50.15 StartY=-31.5 StartZ=0 EndX=50.15 EndY=-1 EndZ=0
    g4: LineSegment StartX=51.15 StartY=-2 StartZ=0 EndX=64.15 EndY=-2 EndZ=0
    g5: LineSegment StartX=64.15 StartY=-2 StartZ=0 EndX=64.15 EndY=-30.5 EndZ=0
    g6: LineSegment StartX=64.15 StartY=-30.5 StartZ=0 EndX=51.15 EndY=-30.5 EndZ=0
    g7: LineSegment StartX=51.15 StartY=-30.5 StartZ=0 EndX=51.15 EndY=-2 EndZ=0
  constraints (22):
    c: Coincident(g0,g1)
    c: Coincident(g1,g2)
    c: Coincident(g2,g3)
    c: Coincident(g3,g0)
    c: Horizontal(g0)
    c: Horizontal(g2)
    c: Vertical(g1)
    c: Vertical(g3)
    c: Coincident(g0,g-3)
    c: Coincident(g1,g-4)
    c: Coincident(g4,g5)
    c: Coincident(g5,g6)
    c: Coincident(g6,g7)
    c: Coincident(g7,g4)
    c: Horizontal(g4)
    c: Horizontal(g6)
    c: Vertical(g5)
    c: Vertical(g7)
    c: DistanceX(g4,g0) = 1
    c: DistanceX(g0,g4) = 1
    c: DistanceY(g2,g6) = 1
    c: DistanceY(g4,g0) = 1
FEATURE [PartDesign::Pad] Pad033
  BaseFeature = -> Pad032
  Length = 15
  Length2 = 100
  Profile = -> Sketch063
  Type = 0
FEATURE [PartDesign::Plane] DatumPlane027
  AttachmentOffset = pos=(0,0,0) rot=(0,1,0;1.5708rad)
  Length = 84.4867
  MapMode = 7
  Placement = pos=(-65.15,-31.5,1) rot=(1,0,0;1.5708rad)
  ResizeMode = 0
  Support = -> [Sketch063]
  Width = 38.3367
FEATURE [PartDesign::Plane] DatumPlane028
  AttachmentOffset = pos=(0,0,15) rot=(0,0,1;0rad)
  Length = 86.3191
  MapMode = 2
  Placement = pos=(0,0,-14) rot=(0,1,0;3.14159rad)
  ResizeMode = 0
  Support = -> [Sketch063]
  Width = 52.6691
  expr: AttachmentOffset.Base.z = Pad033.Length
FEATURE [Sketcher::SketchObject] Sketch064
  ExternalGeometry = -> [Sketch063,DatumPlane028]
  MapMode = 5
  Placement = pos=(-65.15,-31.5,1) rot=(1,0,0;1.5708rad)
  Support = -> [DatumPlane027]
  sketch-geometry (5):
    g0: LineSegment [constr] StartX=15 StartY=-3.2e-15 StartZ=0 EndX=15 EndY=-15 EndZ=0
    g1: LineSegment [constr] StartX=0 StartY=0 StartZ=0 EndX=0 EndY=-15 EndZ=0
    g2: LineSegment StartX=15 StartY=-15 StartZ=0 EndX=0 EndY=-10.9808 EndZ=0
    g3: LineSegment StartX=0 StartY=-10.9808 StartZ=0 EndX=0 EndY=-15 EndZ=0
    g4: LineSegment StartX=0 StartY=-15 StartZ=0 EndX=15 EndY=-15 EndZ=0
  constraints (13):
    c: Coincident(g0,g-4)
    c: PointOnObject(g0,g-5)
    c: Vertical(g0)
    c: Coincident(g1,g-1)
    c: PointOnObject(g1,g-5)
    c: Vertical(g1)
    c: Coincident(g2,g0)
    c: PointOnObject(g2,g1)
    c: Coincident(g3,g2)
    c: Coincident(g3,g1)
    c: Coincident(g4,g3)
    c: Coincident(g4,g2)
    c: Angle(g2,g4) = 0.261799
FEATURE [PartDesign::Pocket] Pocket007016
  BaseFeature = -> Pad033
  Length = 5
  Length2 = 100
  Profile = -> Sketch064
  Type = 1
FEATURE [Sketcher::SketchObject] Sketch065
  ExternalGeometry = -> [Sketch064,Pocket007016]
  MapMode = 5
  Placement = pos=(-6.85941,6.9e-15,-25.5997) rot=(0.991445,0,-0.130526;3.14159rad)
  Support = -> [Pocket007016]
  sketch-geometry (4):
    g0: LineSegment StartX=-60.3469 StartY=1 StartZ=0 EndX=-45.3177 EndY=1 EndZ=0
    g1: LineSegment StartX=-45.3177 StartY=1 StartZ=0 EndX=-45.3177 EndY=30.5 EndZ=0
    g2: LineSegment StartX=-45.3177 StartY=30.5 StartZ=0 EndX=-60.3469 EndY=30.5 EndZ=0
    g3: LineSegment StartX=-60.3469 StartY=30.5 StartZ=0 EndX=-60.3469 EndY=1 EndZ=0
  constraints (10):
    c: Coincident(g0,g1)
    c: Coincident(g1,g2)
    c: Coincident(g2,g3)
    c: Coincident(g3,g0)
    c: Horizontal(g2)
    c: Vertical(g1)
    c: Vertical(g3)
    c: Coincident(g0,g-4)
    c: PointOnObject(g0,g-4)
    c: DistanceX(g0,g-4) = 0.5
FEATURE [PartDesign::Pad] Pad034
  BaseFeature = -> Pocket007016
  Length = 1
  Length2 = 100
  Profile = -> Sketch065
  Reversed = true
  Type = 0
FEATURE [Sketcher::SketchObject] Sketch066
  ExternalGeometry = -> [Pad034]
  MapMode = 5
  Placement = pos=(-50.15,0,0) rot=(0.57735,0.57735,0.57735;2.0944rad)
  Support = -> [Pad034]
  sketch-geometry (4):
    g0: LineSegment StartX=-3 StartY=-8 StartZ=0 EndX=-29.5 EndY=-8 EndZ=0
    g1: LineSegment StartX=-29.5 StartY=-8 StartZ=0 EndX=-29.5 EndY=-13 EndZ=0
    g2: LineSegment StartX=-29.5 StartY=-13 StartZ=0 EndX=-3 EndY=-13 EndZ=0
    g3: LineSegment StartX=-3 StartY=-13 StartZ=0 EndX=-3 EndY=-8 EndZ=0
  constraints (12):
    c: Coincident(g0,g1)
    c: Coincident(g1,g2)
    c: Coincident(g2,g3)
    c: Coincident(g3,g0)
    c: Horizontal(g0)
    c: Horizontal(g2)
    c: Vertical(g1)
    c: Vertical(g3)
    c: DistanceY(g3,g3) = 5
    c: DistanceY(g-3,g2) = 1
    c: DistanceX(g2,g-3) = 2
    c: DistanceX(g-4,g1) = 2
FEATURE [PartDesign::Pocket] Pocket007017
  BaseFeature = -> Pad034
  Length = 3
  Length2 = 100
  Profile = -> Sketch066
  Type = 0
FEATURE [PartDesign::Body] Body004  label="Fanduct_Düse"
  Group = -> [ShapeBinder003,Sketch061,Pad031,Sketch062,Pad032,DatumPlane026,Sketch063,Pad033,DatumPlane027,DatumPlane028,Sketch064,Pocket007016,Sketch065,Pad034,Sketch066,Pocket007017]
  Origin = -> Origin008
  Placement = pos=(0,-32,-16.75) rot=(0,0,1;0rad)
  Tip = -> Pocket007017
FEATURE [Part::Feature] _0mm_Fan003002  label="reference-50mm_Fan005"
  Placement = pos=(-1.5,-35,-54.25) rot=(0.57735,-0.57735,0.57735;4.18879rad)
  shape: bbox 51.49 x 51.5 x 15 mm, 262 faces, 0 solids (baked)
FEATURE [PartDesign::ShapeBinder] ShapeBinder005  label="ShapeBinder_50mm_Fan_Opening"
  Placement = pos=(-1.5,-35,-54.25) rot=(0.57735,-0.57735,0.57735;4.18879rad)
  Support = -> [_0mm_Fan003002]
  TraceSupport = false
FEATURE [Part::Feature] Part__Feature022  label="EX_EXTRUDER_LID (Edition 4)_Public001"
  Placement = pos=(0.461723,-9.23586,-22) rot=(1,0,0;3.14159rad)
  shape: bbox 46.39 x 49.51 x 137 mm, 484 faces (baked)
FEATURE [Part::Mirroring] Part__Mirroring019  label="EX_EXTRUDER_LID (Edition 4)_Public (Mirror #1)001"
  Base = (0,0,0)
  Normal = (1,0,0)
  Placement = pos=(13.5,-18,-29) rot=(0.707107,-0.707107,0;3.14159rad)
  Source = -> Part__Feature022
FEATURE [PartDesign::ShapeBinder] ShapeBinder006  label="ShapeBinder_Titan_Frontblende"
  Support = -> [Part__Mirroring019]
  TraceSupport = false
FEATURE [PartDesign::ShapeBinder] ShapeBinder007  label="ShapeBinder_50_mm_Fan_Front"
  Placement = pos=(-1.5,-35,-54.25) rot=(0.57735,-0.57735,0.57735;4.18879rad)
  Support = -> [_0mm_Fan003002]
  TraceSupport = false
FEATURE [Sketcher::SketchObject] Sketch067
  AttachmentOffset = pos=(0,0,-4) rot=(0,0,1;0rad)
  ExternalGeometry = -> [ShapeBinder006,ShapeBinder007]
  MapMode = 5
  Placement = pos=(0,0,-4) rot=(0,0,1;0rad)
  Support = -> [XY_Plane001]
  sketch-geometry (29):
    g0: Circle [constr] CenterX=21.55 CenterY=10.5171 CenterZ=0 NormalX=0 NormalY=0 NormalZ=1 AngleXU=0 Radius=1.875
    g1: Circle CenterX=21 CenterY=-26.8392 CenterZ=0 NormalX=0 NormalY=0 NormalZ=1 AngleXU=0 Radius=1.875
    g2: Circle CenterX=52 CenterY=-26.8392 CenterZ=0 NormalX=0 NormalY=0 NormalZ=1 AngleXU=0 Radius=1.875
    g3: Circle [constr] CenterX=52 CenterY=4.16075 CenterZ=0 NormalX=0 NormalY=0 NormalZ=1 AngleXU=0 Radius=1.875
    g4: Circle [constr] CenterX=36.5 CenterY=-40 CenterZ=0 NormalX=0 NormalY=0 NormalZ=1 AngleXU=0 Radius=2
    g5: Circle [constr] CenterX=74.5 CenterY=2.48529 CenterZ=0 NormalX=0 NormalY=0 NormalZ=1 AngleXU=0 Radius=2
    g6: LineSegment StartX=17 StartY=-30.8392 StartZ=0 EndX=30.5839 EndY=-30.8392 EndZ=0
    g7: LineSegment StartX=55.2331 StartY=-30.8392 StartZ=0 EndX=83.3368 EndY=5.7886 EndZ=0
    g8: LineSegment StartX=83.3368 StartY=5.7886 StartZ=0 EndX=75.403 EndY=11.876 EndZ=0
    g9: LineSegment StartX=75.403 StartY=11.876 StartZ=0 EndX=48.7669 EndY=-22.8392 EndZ=0
    g10: LineSegment StartX=48.7669 StartY=-22.8392 StartZ=0 EndX=17 EndY=-22.8392 EndZ=0
    g11: LineSegment StartX=17 StartY=-22.8392 StartZ=0 EndX=17 EndY=-30.8392 EndZ=0
    g12: LineSegment [constr] StartX=17 StartY=-26.8392 StartZ=0 EndX=58.3022 EndY=-26.8392 EndZ=0
    g13: LineSegment [constr] StartX=52 StartY=-26.8392 StartZ=0 EndX=79.3699 EndY=8.83228 EndZ=0
    g14: LineSegment [constr] StartX=48.7669 StartY=-22.8392 StartZ=0 EndX=55.2331 EndY=-30.8392 EndZ=0
    g15: LineSegment StartX=30.5839 StartY=-30.8392 StartZ=0 EndX=30.5839 EndY=-41 EndZ=0
    g16: LineSegment StartX=42.4161 StartY=-30.8392 StartZ=0 EndX=42.4161 EndY=-41 EndZ=0
    g17: ArcOfCircle CenterX=36.5 CenterY=-40 CenterZ=0 NormalX=0 NormalY=0 NormalZ=1 AngleXU=0 Radius=6 StartAngle=3.30904 EndAngle=6.11574
    g18: ArcOfCircle CenterX=36.5 CenterY=-35 CenterZ=0 NormalX=0 NormalY=0 NormalZ=1 AngleXU=0 Radius=2.375 StartAngle=1.2e-15 EndAngle=3.14159
    g19: ArcOfCircle CenterX=36.5 CenterY=-41 CenterZ=0 NormalX=0 NormalY=0 NormalZ=1 AngleXU=0 Radius=2.375 StartAngle=3.14159 EndAngle=6.28319
    g20: LineSegment StartX=34.125 StartY=-35 StartZ=0 EndX=34.125 EndY=-41 EndZ=0
    g21: LineSegment StartX=38.875 StartY=-35 StartZ=0 EndX=38.875 EndY=-41 EndZ=0
    g22: LineSegment [constr] StartX=36.5 StartY=-35 StartZ=0 EndX=36.5 EndY=-41 EndZ=0
    g23: LineSegment StartX=42.4161 StartY=-30.8392 StartZ=0 EndX=55.2331 EndY=-30.8392 EndZ=0
    g24: LineSegment [constr] StartX=30.5839 StartY=-41 StartZ=0 EndX=42.4161 EndY=-41 EndZ=0
    g25: ArcOfCircle CenterX=75.7175 CenterY=4.07204 CenterZ=0 NormalX=0 NormalY=0 NormalZ=1 AngleXU=0 Radius=2.375 StartAngle=5.62872 EndAngle=8.77031
    g26: ArcOfCircle CenterX=72.6738 CenterY=0.105174 CenterZ=0 NormalX=0 NormalY=0 NormalZ=1 AngleXU=0 Radius=2.375 StartAngle=2.48713 EndAngle=5.62872
    g27: LineSegment StartX=73.8332 StartY=5.51779 StartZ=0 EndX=70.7895 EndY=1.55092 EndZ=0
    g28: LineSegment StartX=77.6017 StartY=2.62629 StartZ=0 EndX=74.5581 EndY=-1.34057 EndZ=0
  constraints (74):
    c: Coincident(g0,g-3)
    c: Coincident(g1,g-6)
    c: Coincident(g2,g-5)
    c: Coincident(g3,g-4)
    c: Diameter(g-4) = 3.2
    c: Diameter(g3) = 3.75
    c: Equal(g3,g0)
    c: Equal(g3,g1)
    c: Equal(g3,g2)
    c: PointOnObject(g-7,g4)
    c: PointOnObject(g-8,g4)
    c: PointOnObject(g-9,g4)
    c: PointOnObject(g-10,g5)
    c: PointOnObject(g-12,g5)
    c: PointOnObject(g-11,g5)
    c: Horizontal(g6)
    c: Coincident(g23,g7)
    c: Coincident(g7,g8)
    c: Coincident(g8,g9)
    c: Coincident(g9,g10)
    c: Parallel(g9,g7)
    c: Perpendicular(g8,g9)
    c: Horizontal(g10)
    c: Coincident(g11,g10)
    c: Coincident(g11,g6)
    c: Vertical(g11)
    c: PointOnObject(g12,g7)
    c: Symmetric(g6,g10,g12)
    c: PointOnObject(g1,g12)
    c: Coincident(g13,g2)
    c: PointOnObject(g13,g8)
    c: Symmetric(g8,g7,g13)
    c: PointOnObject(g5,g13)
    c: DistanceY(g11,g11) = 8
    c: Coincident(g14,g9)
    c: Coincident(g14,g23)
    c: Distance(g8) = 10
    c: Vertical(g15)
    c: Vertical(g16)
    c: Coincident(g17,g4)
    c: Coincident(g17,g16)
    c: Coincident(g15,g17)
    c: Tangent(g18,g21) = 1.5708
    c: Tangent(g18,g20) = -1.5708
    c: Tangent(g20,g19) = -1.5708
    c: Tangent(g21,g19) = 1.5708
    c: Vertical(g20)
    c: Equal(g18,g19)
    c: Coincident(g22,g18)
    c: Coincident(g22,g19)
    c: Coincident(g6,g15)
    c: Coincident(g23,g16)
    c: Tangent(g6,g23)
    c: Coincident(g24,g15)
    c: Coincident(g24,g16)
    c: Symmetric(g15,g16,g22)
    c: Diameter(g18) = 4.75
    c: Diameter(g17) = 12
    c: PointOnObject(g19,g24)
    c: PointOnObject(g12,g11)
    c: DistanceX(g10,g1) = 4
    c: Distance(g5,g13) = 8
    c: DistanceY(g19,g17) = 1
    c: DistanceY(g20,g20) = 6
    c: Tangent(g25,g28) = 1.5708
    c: Tangent(g25,g27) = -1.5708
    c: Tangent(g27,g26) = -1.5708
    c: Tangent(g28,g26) = 1.5708
    c: Equal(g25,g26)
    c: PointOnObject(g25,g13)
    c: PointOnObject(g26,g13)
    c: Diameter(g26) = 4.75
    c: Distance(g25,g26) = 5
    c: PointOnObject(g25,g5)
FEATURE [PartDesign::Pad] Pad035
  Length = 4.75
  Length2 = 100
  Profile = -> Sketch067
  Type = 3
  UpToFace = -> ShapeBinder007 [Face1]
FEATURE [Sketcher::SketchObject] Sketch068
  ExternalGeometry = -> [ShapeBinder006]
  MapMode = 5
  Placement = pos=(-1.5,-35,0.75) rot=(0.707107,0.707107,0;3.14159rad)
  Support = -> [ShapeBinder007]
  sketch-geometry (2):
    g0: Circle CenterX=8.35304 CenterY=53.5948 CenterZ=0 NormalX=0 NormalY=0 NormalZ=1 AngleXU=0 Radius=3
    g1: Circle CenterX=8.16075 CenterY=22.5 CenterZ=0 NormalX=0 NormalY=0 NormalZ=1 AngleXU=0 Radius=3
  constraints (2):
    c: Diameter(g0) = 6
    c: Equal(g0,g1)
FEATURE [PartDesign::Pocket] Pocket007018
  BaseFeature = -> Pad035
  Length = 3.75
  Length2 = 100
  Profile = -> Sketch068
  Reversed = true
  Type = 0
  expr: Length = Pad035.Length - 1mm
FEATURE [Sketcher::SketchObject] Sketch069
  AttachmentOffset = pos=(0,0,-4) rot=(0,0,1;0rad)
  ExternalGeometry = -> [Sketch067]
  MapMode = 5
  Placement = pos=(0,0,-4) rot=(0,0,1;0rad)
  Support = -> [XY_Plane001]
  sketch-geometry (24):
    g0: LineSegment StartX=40.125 StartY=-37.0929 StartZ=0 EndX=40.125 EndY=-32.9071 EndZ=0
    g1: LineSegment StartX=40.125 StartY=-32.9071 StartZ=0 EndX=36.5 EndY=-30.8142 EndZ=0
    g2: LineSegment StartX=36.5 StartY=-30.8142 StartZ=0 EndX=32.875 EndY=-32.9071 EndZ=0
    g3: LineSegment StartX=32.875 StartY=-32.9071 StartZ=0 EndX=32.875 EndY=-37.0929 EndZ=0
    g4: Circle [constr] CenterX=36.5 CenterY=-35 CenterZ=0 NormalX=0 NormalY=0 NormalZ=1 AngleXU=0 Radius=4.18579
    g5: LineSegment StartX=40.125 StartY=-43.0929 StartZ=0 EndX=40.125 EndY=-38.9071 EndZ=0
    g6: LineSegment StartX=32.875 StartY=-38.9071 StartZ=0 EndX=32.875 EndY=-43.0929 EndZ=0
    g7: LineSegment StartX=32.875 StartY=-43.0929 StartZ=0 EndX=36.5 EndY=-45.1858 EndZ=0
    g8: LineSegment StartX=36.5 StartY=-45.1858 StartZ=0 EndX=40.125 EndY=-43.0929 EndZ=0
    g9: Circle [constr] CenterX=36.5 CenterY=-41 CenterZ=0 NormalX=0 NormalY=0 NormalZ=1 AngleXU=0 Radius=4.18579
    g10: LineSegment StartX=32.875 StartY=-37.0929 StartZ=0 EndX=32.875 EndY=-38.9071 EndZ=0
    g11: LineSegment StartX=77.3194 StartY=0.204926 StartZ=0 EndX=79.8675 EndY=3.52582 EndZ=0
    g12: LineSegment StartX=79.8675 StartY=3.52582 StartZ=0 EndX=78.2655 EndY=7.39293 EndZ=0
    g13: LineSegment StartX=78.2655 StartY=7.39293 StartZ=0 EndX=74.1155 EndY=7.93915 EndZ=0
    g14: LineSegment StartX=74.1155 StartY=7.93915 StartZ=0 EndX=71.5675 EndY=4.61826 EndZ=0
    g15: Circle [constr] CenterX=75.7175 CenterY=4.07204 CenterZ=0 NormalX=0 NormalY=0 NormalZ=1 AngleXU=0 Radius=4.18579
    g16: LineSegment StartX=71.0718 StartY=3.97229 StartZ=0 EndX=68.5238 EndY=0.651395 EndZ=0
    g17: LineSegment StartX=68.5238 StartY=0.651395 StartZ=0 EndX=70.1258 EndY=-3.21572 EndZ=0
    g18: LineSegment StartX=70.1258 StartY=-3.21572 StartZ=0 EndX=74.2758 EndY=-3.76194 EndZ=0
    g19: LineSegment StartX=74.2758 StartY=-3.76194 StartZ=0 EndX=76.8238 EndY=-0.441047 EndZ=0
    g20: Circle [constr] CenterX=72.6738 CenterY=0.105174 CenterZ=0 NormalX=0 NormalY=0 NormalZ=1 AngleXU=0 Radius=4.18579
    g21: LineSegment StartX=77.3194 StartY=0.204926 StartZ=0 EndX=76.8238 EndY=-0.441047 EndZ=0
    g22: LineSegment StartX=71.5675 StartY=4.61826 StartZ=0 EndX=71.0718 EndY=3.97229 EndZ=0
    g23: LineSegment StartX=40.125 StartY=-37.0929 StartZ=0 EndX=40.125 EndY=-38.9071 EndZ=0
  constraints (74):
    c: Coincident(g7,g6)
    c: Coincident(g10,g6)
    c: Coincident(g10,g3)
    c: Coincident(g3,g2)
    c: Coincident(g8,g7)
    c: Coincident(g2,g1)
    c: Coincident(g8,g5)
    c: Coincident(g1,g0)
    c: Coincident(g11,g12)
    c: Coincident(g12,g13)
    c: Coincident(g13,g14)
    c: Equal(g11,g12)
    c: Equal(g11,g13)
    c: Equal(g11,g14)
    c: PointOnObject(g11,g15)
    c: PointOnObject(g12,g15)
    c: PointOnObject(g13,g15)
    c: PointOnObject(g14,g15)
    c: Coincident(g16,g17)
    c: Coincident(g17,g18)
    c: Coincident(g18,g19)
    c: PointOnObject(g16,g20)
    c: PointOnObject(g16,g20)
    c: PointOnObject(g17,g20)
    c: PointOnObject(g18,g20)
    c: PointOnObject(g19,g20)
    c: Equal(g15,g20)
    c: Distance(g18,g16) = 7.25
    c: Parallel(g16,g-5)
    c: Parallel(g14,g-5)
    c: Coincident(g15,g-6)
    c: Coincident(g-7,g20)
    c: Coincident(g4,g-4)
    c: Coincident(g9,g-3)
    c: PointOnObject(g0,g4)
    c: PointOnObject(g1,g4)
    c: PointOnObject(g2,g4)
    c: PointOnObject(g3,g4)
    c: PointOnObject(g6,g9)
    c: PointOnObject(g6,g9)
    c: PointOnObject(g7,g9)
    c: PointOnObject(g5,g9)
    c: PointOnObject(g5,g9)
    c: PointOnObject(g0,g4)
    c: Distance(g0,g2) = 7.25
    c: Equal(g1,g2)
    c: Equal(g2,g7)
    c: Equal(g7,g8)
    c: Equal(g0,g3)
    c: Equal(g3,g6)
    c: Equal(g6,g5)
    c: Equal(g1,g0)
    c: Equal(g5,g0)
    c: Equal(g6,g3)
    c: Equal(g8,g7)
    c: Coincident(g21,g19)
    c: PointOnObject(g11,g15)
    c: Coincident(g21,g11)
    c: Coincident(g16,g22)
    c: Coincident(g14,g22)
    c: Equal(g12,g13)
    c: Equal(g13,g14)
    c: Equal(g14,g16)
    c: Equal(g16,g17)
    c: Equal(g17,g18)
    c: Equal(g18,g19)
    c: Equal(g19,g11)
    c: Parallel(g21,g19)
    c: Parallel(g1,g7)
    c: Coincident(g23,g0)
    c: Coincident(g23,g5)
    c: Vertical(g23)
    c: Vertical(g0)
    c: Vertical(g3)
FEATURE [PartDesign::Pocket] Pocket007019
  BaseFeature = -> Pocket007018
  Length = 3.5
  Length2 = 100
  Profile = -> Sketch069
  Reversed = true
  Type = 0
FEATURE [PartDesign::Plane] DatumPlane029
  Length = 61.8322
  MapMode = 5
  Placement = pos=(29.5,-35,-54.25) rot=(0.57735,-0.57735,-0.57735;2.0944rad)
  ResizeMode = 0
  Support = -> [ShapeBinder005]
  Width = 81.8322
FEATURE [Sketcher::SketchObject] Sketch070
  ExternalGeometry = -> [ShapeBinder005]
  MapMode = 5
  Placement = pos=(29.5,-35,-54.25) rot=(0.57735,-0.57735,-0.57735;2.0944rad)
  Support = -> [DatumPlane029]
  expr: Constraints[26] = Constraints.Wandstärke
  expr: Constraints[24] = Constraints.Clearance
  sketch-geometry (10):
    g0: LineSegment StartX=-40.6 StartY=68.6 StartZ=0 EndX=-24.4 EndY=68.6 EndZ=0
    g1: LineSegment StartX=-24.4 StartY=68.6 StartZ=0 EndX=-24.4 EndY=56.4 EndZ=0
    g2: LineSegment StartX=-24.4 StartY=56.4 StartZ=0 EndX=-40.6 EndY=56.4 EndZ=0
    g3: LineSegment StartX=-40.6 StartY=56.4 StartZ=0 EndX=-40.6 EndY=68.6 EndZ=0
    g4: LineSegment StartX=-40 StartY=68 StartZ=0 EndX=-25 EndY=68 EndZ=0
    g5: LineSegment StartX=-25 StartY=68 StartZ=0 EndX=-25 EndY=57 EndZ=0
    g6: LineSegment StartX=-25 StartY=57 StartZ=0 EndX=-40 EndY=57 EndZ=0
    g7: LineSegment StartX=-40 StartY=57 StartZ=0 EndX=-40 EndY=68 EndZ=0
    g8: LineSegment [constr] StartX=-32.5 StartY=69 StartZ=0 EndX=-32.5 EndY=56 EndZ=0
    g9: LineSegment [constr] StartX=-41 StartY=62.5 StartZ=0 EndX=-24 EndY=62.5 EndZ=0
  constraints (28):
    c: DistanceX(g-5,g-6) = 17
    c: DistanceY(g-6,g-6) = 13
    c: Coincident(g0,g1)
    c: Coincident(g1,g2)
    c: Coincident(g2,g3)
    c: Coincident(g3,g0)
    c: Horizontal(g0)
    c: Vertical(g3)
    c: Coincident(g4,g5)
    c: Coincident(g5,g6)
    c: Coincident(g6,g7)
    c: Coincident(g7,g4)
    c: Horizontal(g4)
    c: Vertical(g7)
    c: PointOnObject(g8,g-3)
    c: PointOnObject(g9,g-5)
    c: PointOnObject(g9,g-6)
    c: Symmetric(g-6,g-6,g9)
    c: Symmetric(g-5,g-6,g8)
    c: Symmetric(g0,g1,g9)
    c: Symmetric(g4,g5,g9)
    c: Symmetric(g1,g2,g8)
    c: Symmetric(g6,g5,g8)
    c: DistanceX(g0,g-6) = 0.4  'Clearance'
    c: DistanceY(g0,g-6) = 0.4
    c: DistanceY(g4,g0) = 0.6  'Wandstärke'
    c: DistanceX(g4,g0) = 0.6
    c: PointOnObject(g8,g-4)
FEATURE [Sketcher::SketchObject] Sketch071
  AttachmentOffset = pos=(0,0,-2) rot=(0,0,1;0rad)
  ExternalGeometry = -> [Sketch070]
  MapMode = 5
  Placement = pos=(0,0,-2) rot=(0,0,1;0rad)
  Support = -> [XY_Plane010]
  expr: Constraints[2] = SnugglyFit.Length
  sketch-geometry (4):
    g0: LineSegment [constr] StartX=-24.4 StartY=-69.6 StartZ=0 EndX=-17.4 EndY=-69.6 EndZ=0
    g1: LineSegment StartX=-22.4 StartY=-69.6 StartZ=0 EndX=-17.4 EndY=-59.6 EndZ=0
    g2: LineSegment StartX=-17.4 StartY=-59.6 StartZ=0 EndX=-17.4 EndY=-69.6 EndZ=0
    g3: LineSegment StartX=-17.4 StartY=-69.6 StartZ=0 EndX=-22.4 EndY=-69.6 EndZ=0
  constraints (11):
    c: Coincident(g0,g-4)
    c: Horizontal(g0)
    c: DistanceX(g0,g0) = 7
    c: PointOnObject(g1,g0)
    c: Coincident(g1,g2)
    c: Coincident(g2,g3)
    c: Coincident(g3,g1)
    c: Vertical(g2)
    c: DistanceX(g0,g1) = 2
    c: Coincident(g2,g0)
    c: DistanceY(g2,g2) = 10
FEATURE [Sketcher::SketchObject] Sketch072
  ExternalGeometry = -> [ShapeBinder005,Sketch070]
  MapMode = 5
  Placement = pos=(29.5,-35,-54.25) rot=(0.57735,-0.57735,-0.57735;2.0944rad)
  Support = -> [DatumPlane029]
  sketch-geometry (8):
    g0: LineSegment StartX=-42 StartY=70 StartZ=0 EndX=-23 EndY=70 EndZ=0
    g1: LineSegment StartX=-23 StartY=70 StartZ=0 EndX=-23 EndY=55 EndZ=0
    g2: LineSegment StartX=-23 StartY=55 StartZ=0 EndX=-42 EndY=55 EndZ=0
    g3: LineSegment StartX=-42 StartY=55 StartZ=0 EndX=-42 EndY=70 EndZ=0
    g4: LineSegment StartX=-40 StartY=68 StartZ=0 EndX=-25 EndY=68 EndZ=0
    g5: LineSegment StartX=-25 StartY=68 StartZ=0 EndX=-25 EndY=57 EndZ=0
    g6: LineSegment StartX=-25 StartY=57 StartZ=0 EndX=-40 EndY=57 EndZ=0
    g7: LineSegment StartX=-40 StartY=57 StartZ=0 EndX=-40 EndY=68 EndZ=0
  constraints (20):
    c: Coincident(g0,g1)
    c: Coincident(g1,g2)
    c: Coincident(g2,g3)
    c: Coincident(g3,g0)
    c: Horizontal(g0)
    c: Horizontal(g2)
    c: Vertical(g1)
    c: Vertical(g3)
    c: Coincident(g0,g-3)
    c: Coincident(g1,g-4)
    c: Coincident(g4,g5)
    c: Coincident(g5,g6)
    c: Coincident(g6,g7)
    c: Coincident(g7,g4)
    c: Horizontal(g4)
    c: Horizontal(g6)
    c: Vertical(g5)
    c: Vertical(g7)
    c: Coincident(g5,g-6)
    c: Coincident(g4,g-5)
FEATURE [PartDesign::Plane] DatumPlane030  label="DatumPlane_Fan_Adapter"
  Length = 35.5588
  MapMode = 5
  Placement = pos=(15,0,0) rot=(0.57735,0.57735,0.57735;2.0944rad)
  ResizeMode = 0
  Support = -> [ShapeBinder]
  Width = 31.3088
FEATURE [Sketcher::SketchObject] Sketch073  label="Loft_Unten"
  ExternalGeometry = -> [ShapeBinder]
  MapMode = 5
  Placement = pos=(15,0,0) rot=(0.57735,0.57735,0.57735;2.0944rad)
  Support = -> [DatumPlane030]
  sketch-geometry (10):
    g0: LineSegment [constr] StartX=-10 StartY=5.5 StartZ=0 EndX=10 EndY=5.5 EndZ=0
    g1: LineSegment [constr] StartX=-1.8e-15 StartY=10 StartZ=0 EndX=-2.6e-15 EndY=1 EndZ=0
    g2: LineSegment StartX=-11 StartY=12 StartZ=0 EndX=11 EndY=12 EndZ=0
    g3: LineSegment StartX=11 StartY=12 StartZ=0 EndX=11 EndY=0 EndZ=0
    g4: LineSegment StartX=11 StartY=0 StartZ=0 EndX=-11 EndY=0 EndZ=0
    g5: LineSegment StartX=-11 StartY=0 StartZ=0 EndX=-11 EndY=12 EndZ=0
    g6: LineSegment StartX=-10 StartY=10 StartZ=0 EndX=10 EndY=10 EndZ=0
    g7: LineSegment StartX=10 StartY=10 StartZ=0 EndX=10 EndY=1 EndZ=0
    g8: LineSegment StartX=10 StartY=1 StartZ=0 EndX=-10 EndY=1 EndZ=0
    g9: LineSegment StartX=-10 StartY=1 StartZ=0 EndX=-10 EndY=10 EndZ=0
  constraints (27):
    c: PointOnObject(g0,g-5)
    c: PointOnObject(g0,g-6)
    c: PointOnObject(g1,g-3)
    c: PointOnObject(g1,g-4)
    c: Symmetric(g-6,g-5,g1)
    c: Symmetric(g-6,g-6,g0)
    c: Coincident(g2,g3)
    c: Coincident(g3,g4)
    c: Coincident(g4,g5)
    c: Coincident(g5,g2)
    c: Horizontal(g4)
    c: Vertical(g5)
    c: Symmetric(g2,g2,g1)
    c: DistanceX(g2,g-6) = -1  'clearance'
    c: Coincident(g6,g7)
    c: Coincident(g7,g8)
    c: Coincident(g8,g9)
    c: Coincident(g9,g6)
    c: Horizontal(g6)
    c: Vertical(g9)
    c: Distance(g7) = 9
    c: Symmetric(g7,g6,g0)
    c: Symmetric(g7,g8,g1)
    c: Coincident(g7,g-6)
    c: PointOnObject(g2,g-8)
    c: PointOnObject(g4,g-7)
    c: Vertical(g3)
FEATURE [PartDesign::ShapeBinder] ShapeBinder008  label="ShapeBinder_30mm_Fan_Adapter001"
  Support = -> [Pocket001]
  TraceSupport = false
FEATURE [PartDesign::ShapeBinder] ShapeBinder009  label="ShapeBinder_50mm_Fan_Opening001"
  Placement = pos=(-1.5,-35,-54.25) rot=(0.57735,-0.57735,0.57735;4.18879rad)
  Support = -> [_0mm_Fan003002]
  TraceSupport = false
FEATURE [Part::Loft] Loft  label="Loft-unused"
  Closed = false
  MaxDegree = 5
  Ruled = false
  Sections = -> [ShapeBinder008,ShapeBinder009]
  Solid = false
FEATURE [PartDesign::FeatureBase] BaseFeature
  BaseFeature = -> Loft
FEATURE [PartDesign::Pad] Pad036  label="SnugglyFit"
  BaseFeature = -> BaseFeature
  Length = 7
  Length2 = 100
  Profile = -> Sketch070
  Reversed = true
  Type = 0
FEATURE [PartDesign::Pocket] Pocket007020  label="Cutout_Fan_Rim"
  BaseFeature = -> Pad036
  Length = 3
  Length2 = 100
  Midplane = true
  Profile = -> Sketch071
  Reversed = true
  Type = 0
FEATURE [PartDesign::Pad] Pad037  label="Kragen"
  BaseFeature = -> Pocket007020
  Length = 0.5
  Length2 = 100
  Profile = -> Sketch072
  Type = 0
FEATURE [PartDesign::Plane] DatumPlane032  label="DatumPlane032_KragenUnten"
  AttachmentOffset = pos=(0,0,0.5) rot=(0,0,1;0rad)
  Length = 61.8322
  MapMode = 2
  Placement = pos=(29,-35,-54.25) rot=(0.57735,-0.57735,-0.57735;2.0944rad)
  ResizeMode = 0
  Support = -> [Sketch072]
  Width = 81.8322
  expr: AttachmentOffset.Base.z = Kragen.Length
FEATURE [Sketcher::SketchObject] Sketch074  label="Kragen_Unten_Loft_Oben"
  ExternalGeometry = -> [Sketch072]
  MapMode = 5
  Placement = pos=(29,-35,-54.25) rot=(0.57735,-0.57735,-0.57735;2.0944rad)
  Support = -> [DatumPlane032]
  sketch-geometry (8):
    g0: LineSegment StartX=-42 StartY=70 StartZ=0 EndX=-23 EndY=70 EndZ=0
    g1: LineSegment StartX=-23 StartY=70 StartZ=0 EndX=-23 EndY=55 EndZ=0
    g2: LineSegment StartX=-23 StartY=55 StartZ=0 EndX=-42 EndY=55 EndZ=0
    g3: LineSegment StartX=-42 StartY=55 StartZ=0 EndX=-42 EndY=70 EndZ=0
    g4: LineSegment StartX=-40 StartY=68 StartZ=0 EndX=-25 EndY=68 EndZ=0
    g5: LineSegment StartX=-25 StartY=68 StartZ=0 EndX=-25 EndY=57 EndZ=0
    g6: LineSegment StartX=-25 StartY=57 StartZ=0 EndX=-40 EndY=57 EndZ=0
    g7: LineSegment StartX=-40 StartY=57 StartZ=0 EndX=-40 EndY=68 EndZ=0
  constraints (20):
    c: Coincident(g0,g1)
    c: Coincident(g1,g2)
    c: Coincident(g2,g3)
    c: Coincident(g3,g0)
    c: Horizontal(g0)
    c: Horizontal(g2)
    c: Vertical(g1)
    c: Vertical(g3)
    c: Coincident(g0,g-6)
    c: Coincident(g1,g-5)
    c: Coincident(g4,g5)
    c: Coincident(g5,g6)
    c: Coincident(g6,g7)
    c: Coincident(g7,g4)
    c: Horizontal(g4)
    c: Horizontal(g6)
    c: Vertical(g5)
    c: Vertical(g7)
    c: Coincident(g5,g-4)
    c: Coincident(g-3,g4)
FEATURE [PartDesign::AdditiveLoft] AdditiveLoft
  BaseFeature = -> Pad037
  Closed = false
  Profile = -> Sketch074
  Ruled = false
  Sections = -> [Sketch073]
FEATURE [PartDesign::Body] Body007  label="Luftkanal"
  BaseFeature = -> Loft
  Group = -> [BaseFeature,ShapeBinder,ShapeBinder005,DatumPlane029,Sketch070,Pad036,Sketch071,Pocket007020,Sketch072,Pad037,DatumPlane030,DatumPlane032,Sketch074,Sketch073,AdditiveLoft]
  Origin = -> Origin010
  Tip = -> AdditiveLoft
FEATURE [PartDesign::Fillet] Fillet001
  Base = -> Pocket007019 [Edge4,Edge2,Edge36,Edge58,Edge60,Edge62,Edge61,Edge59]
  BaseFeature = -> Pocket007019
  Radius = 3
FEATURE [PartDesign::Body] Body001  label="Fanattachment-Titan-design"
  Group = -> [ShapeBinder007,ShapeBinder006,Sketch067,Pad035,Sketch068,Pocket007018,Sketch069,Pocket007019,Fillet001]
  Origin = -> Origin001
  Tip = -> Fillet001
FEATURE [PartDesign::FeatureBase] Clone
  BaseFeature = -> Body001
FEATURE [PartDesign::Body] Body008  label="Fanattachment-Titan"
  BaseFeature = -> Body001
  Group = -> [Clone]
  Origin = -> Origin011
  Placement = pos=(0,0,0) rot=(1,0,0;3.14159rad)
  Tip = -> Clone
FEATURE [App::Part] Part003  label="3rd-party-interfaces"
  Group = -> [Part__Feature022,Part__Mirroring019,_0mm_Fan003002]
  Origin = -> Origin012
FEATURE [Mesh::Feature] V6_6_Duct  label="V6.6_Duct"
  Placement = pos=(-34.9,-40.25,-13.35) rot=(-0.57735,-0.57735,-0.57735;4.18879rad)
FEATURE [App::DocumentObjectGroup] Gruppe  label="3rd-party001"
  Group = -> [Part001,Fusion001,_0mm_Fan003002,V6_6_Duct]
FEATURE [Part::FeaturePython] BooleanFragments  # WARN: FeaturePython — macro-defined, semantics opaque (R4)
  Mode = 0
  Objects = -> [Body007,Body]
  Tolerance = 0
FEATURE [App::Part] Part004  label="Fanadapter-30mm-Radial-design"
  Group = -> [ShapeBinder008,ShapeBinder009,Loft,Body007,Body,BooleanFragments]
  Origin = -> Origin013
FEATURE [App::Part] Part002  label="Design"
  Group = -> [Body001,Part003,Part004]
  Origin = -> Origin009
  Placement = pos=(-35,-55.25,1.5) rot=(0.57735,-0.57735,0.57735;2.0944rad)
FEATURE [PartDesign::FeatureBase] Clone001
  BaseFeature = -> BooleanFragments
FEATURE [PartDesign::Body] Body009  label="Fanadapter-30mm-Radial"
  Group = -> [Clone001]
  Origin = -> Origin014
  Placement = pos=(25,-5.6e-15,5.6e-15) rot=(-0.57735,-0.57735,-0.57735;2.0944rad)
  Tip = -> Clone001
FEATURE [App::DocumentObjectGroup] Gruppe001  label="printables"
  Group = -> [Body008,Body009]
FEATURE [Part::Feature] Pocket007014001  label="TitanCarrier"
  Placement = pos=(0,0,0) rot=(1,0,0;1.5708rad)
  shape: bbox 103 x 48 x 58 mm, 135 faces (baked)
FEATURE [App::Part] Part  label="Assembly"
  Group = -> [Body003,Body004,Group,Pocket007014001]
  Origin = -> Origin002
